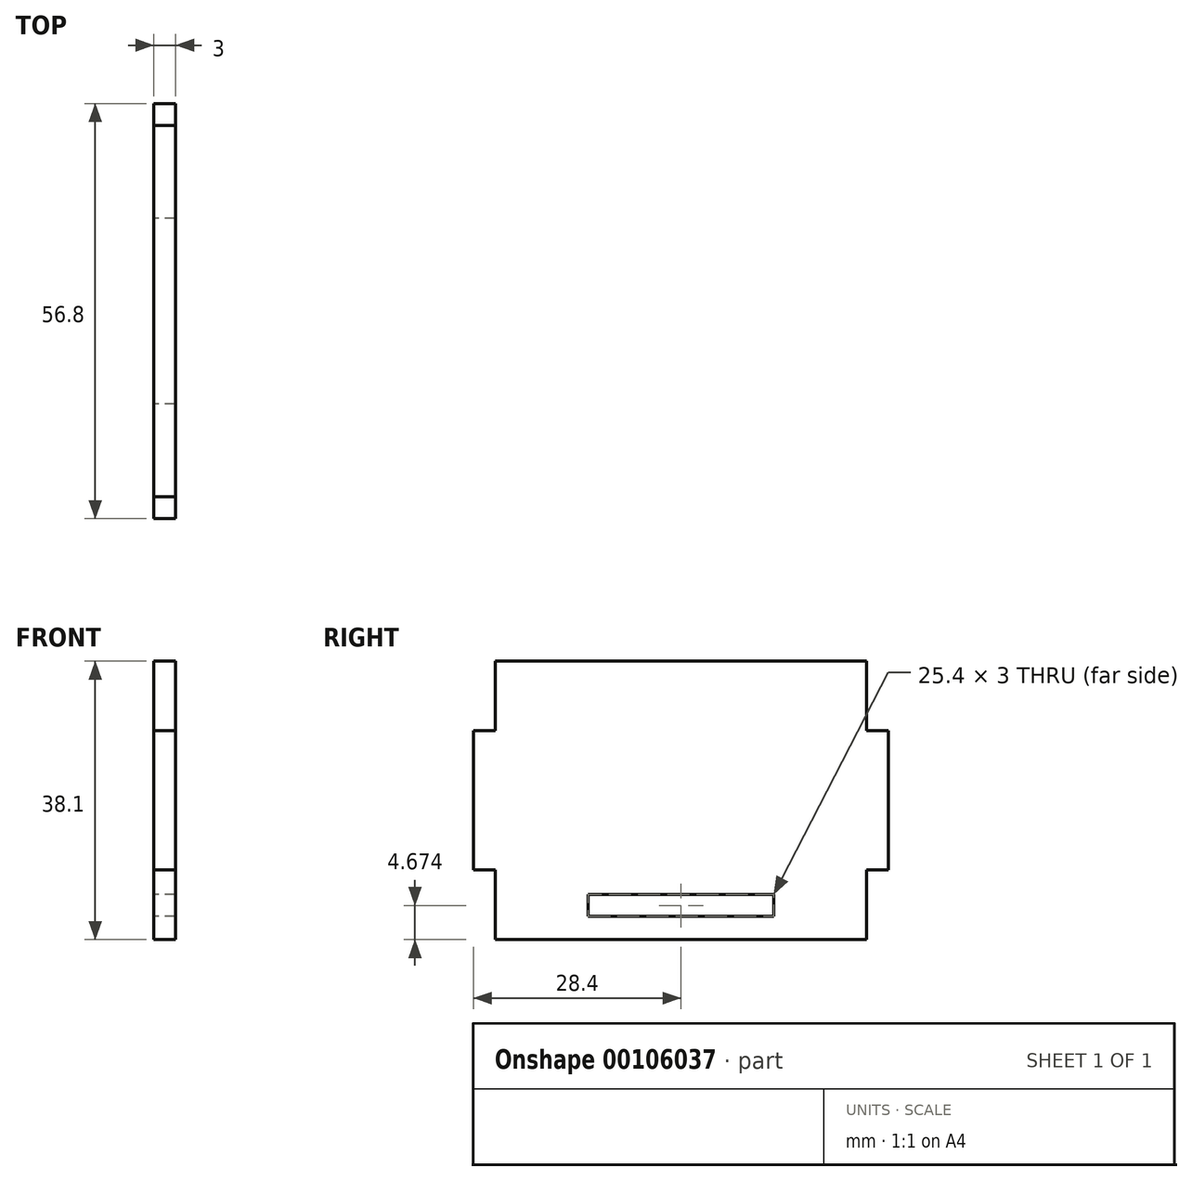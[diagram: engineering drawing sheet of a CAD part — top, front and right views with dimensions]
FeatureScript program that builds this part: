
annotation { "Feature Type Name" : "Feature", "Feature Type Description" : "" }
export const myFeature = defineFeature(function(context is Context, id is Id, definition is map)
    precondition{}
    {
        {
            var Q0;
            Q0=qCreatedBy(makeId("Right.planeOp"),FACE);
            var sketch = newSketch(context, id + "F0", { "sketchPlane" : qUnion([Q0])});
            skPoint(sketch, "E0.middle", {"position": v(0, 0) * mm});
            skLineSegment(sketch, "E1", {"start": v(-28.4, 9.53) * mm, "end": v(-25.4, 9.53) * mm});
            skLineSegment(sketch, "E2", {"start": v(-25.4, 9.53) * mm, "end": v(-25.4, 19.05) * mm});
            skLineSegment(sketch, "E3", {"start": v(-28.4, -9.52) * mm, "end": v(-25.4, -9.52) * mm});
            skLineSegment(sketch, "E4", {"start": v(-25.4, -9.53) * mm, "end": v(-25.4, -19.05) * mm});
            skLineSegment(sketch, "E5", {"start": v(-28.4, 9.53) * mm, "end": v(-28.4, -9.53) * mm});
            skLineSegment(sketch, "E6", {"start": v(-25.4, 19.05) * mm, "end": v(0, 19.05) * mm});
            skLineSegment(sketch, "E7", {"start": v(-25.4, -19.05) * mm, "end": v(0, -19.05) * mm});
            skLineSegment(sketch, "E8", {"start": v(0, -12.88) * mm, "end": v(-12.7, -12.88) * mm});
            skLineSegment(sketch, "E9", {"start": v(-12.7, -12.88) * mm, "end": v(-12.7, -15.88) * mm});
            skLineSegment(sketch, "E10", {"start": v(-12.7, -15.88) * mm, "end": v(0, -15.88) * mm});
            skLineSegment(sketch, "E11.MirrorCS", {"start": v(12.7, -12.88) * mm, "end": v(12.7, -15.88) * mm});
            skLineSegment(sketch, "E12.MirrorCS", {"start": v(28.4, 9.53) * mm, "end": v(25.4, 9.53) * mm});
            skLineSegment(sketch, "E13.MirrorCS", {"start": v(28.4, -9.52) * mm, "end": v(25.4, -9.52) * mm});
            skLineSegment(sketch, "E14.MirrorCS", {"start": v(25.4, 19.05) * mm, "end": v(0, 19.05) * mm});
            skLineSegment(sketch, "E15.MirrorCS", {"start": v(28.4, 9.53) * mm, "end": v(28.4, -9.53) * mm});
            skLineSegment(sketch, "E16.MirrorCS", {"start": v(25.4, -9.53) * mm, "end": v(25.4, -19.05) * mm});
            skLineSegment(sketch, "E17.MirrorCS", {"start": v(25.4, 9.53) * mm, "end": v(25.4, 19.05) * mm});
            skLineSegment(sketch, "E18.MirrorCS", {"start": v(12.7, -15.88) * mm, "end": v(0, -15.88) * mm});
            skLineSegment(sketch, "E19.MirrorCS", {"start": v(25.4, -19.05) * mm, "end": v(0, -19.05) * mm});
            skLineSegment(sketch, "E20.MirrorCS", {"start": v(0, -12.88) * mm, "end": v(12.7, -12.88) * mm});
            skSolve(sketch);
        }
        {
            var Q0;
            Q0=makeQuery(id+"F0.imprint","IMPRINT",FACE,{"disambiguationData":[TD([[makeQuery(id+"F0.imprint","IMPRINT",EDGE,{"derivedFrom":sQuery(id+"F0.wireOp",EDGE,"E1")}),-1.0]])]});
            extrude(context, id + "F1", {"entities" : qUnion([Q0]), "depth" : 3 * mm});
        }
    });
